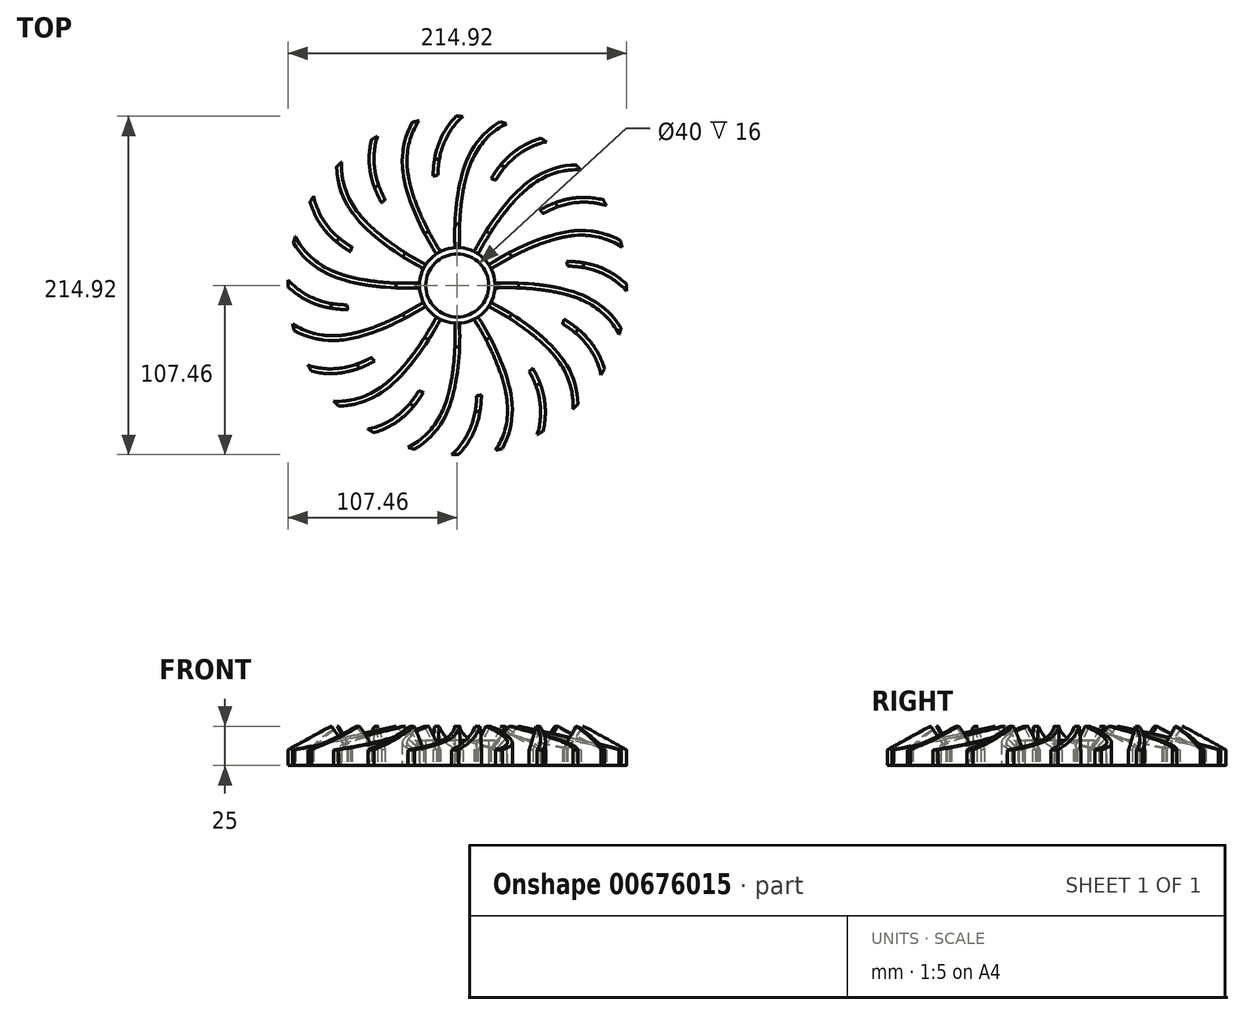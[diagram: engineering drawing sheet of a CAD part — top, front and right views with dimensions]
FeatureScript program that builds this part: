
annotation { "Feature Type Name" : "Feature", "Feature Type Description" : "" }
export const myFeature = defineFeature(function(context is Context, id is Id, definition is map)
    precondition{}
    {
        {
            var Q0;
            Q0=qCreatedBy(makeId("Top.planeOp"),FACE);
            var sketch = newSketch(context, id + "F0", { "sketchPlane" : qUnion([Q0])});
            skCircle(sketch, "E0", {"center": v(0, 0) * mm, "radius": 20 * mm});
            skArc(sketch, "E1", {"start": v(96, -28) * mm, "mid": v(71.3, -7.4) * mm, "end": v(40, 0) * mm});
            skArc(sketch, "E2.0", {"start": v(93.6, -29.8) * mm, "mid": v(69.96, -10.07) * mm, "end": v(40, -3) * mm});
            skLineSegment(sketch, "E3", {"start": v(40, 0) * mm, "end": v(40, -3) * mm});
            skLineSegment(sketch, "E4", {"start": v(93.6, -29.8) * mm, "end": v(96, -28) * mm});
            skCircle(sketch, "E5", {"center": v(0, 0) * mm, "radius": 24 * mm});
            skLineSegment(sketch, "E6", {"start": v(0, 24) * mm, "end": v(0, 20) * mm, "construction": true});
            skLineSegment(sketch, "E7", {"start": v(64.84, -4.56) * mm, "end": v(63.78, -7.36) * mm});
            skLineSegment(sketch, "E8", {"start": v(40, 0) * mm, "end": v(40, -70) * mm, "construction": true});
            skFitSpline(sketch, "E9", {"points": [v(24, 0) * mm, v(83, -9.5) * mm, v(106, -36.5) * mm], "startDerivative": vector(103.5, 1.7) * mm, "endDerivative": vector(16.54, -68.53) * mm, "construction": true});
            skLineSegment(sketch, "E10", {"start": v(-53.16, 0) * mm, "end": v(120.42, 0) * mm, "construction": true});
            skFitSpline(sketch, "E11.0", {"points": [v(23.98, 1.5) * mm, v(28.3, 1.57) * mm, v(37.36, 1.54) * mm, v(49.06, 0.79) * mm, v(58.28, -0.42) * mm, v(65.05, -1.67) * mm, v(71.58, -3.31) * mm, v(77.78, -5.4) * mm, v(83.57, -7.97) * mm, v(88.84, -11.08) * mm, v(93.54, -14.64) * mm, v(97.64, -18.56) * mm, v(101.12, -22.75) * mm, v(104.9, -28.6) * mm, v(106.73, -33.14) * mm, v(107.46, -36.15) * mm]});
            skFitSpline(sketch, "E12.0", {"points": [v(24.02, -1.5) * mm, v(28.32, -1.43) * mm, v(37.27, -1.46) * mm, v(48.79, -2.2) * mm, v(57.82, -3.38) * mm, v(64.42, -4.6) * mm, v(70.74, -6.2) * mm, v(76.7, -8.2) * mm, v(82.2, -10.65) * mm, v(87.17, -13.58) * mm, v(91.6, -16.93) * mm, v(95.45, -20.61) * mm, v(98.7, -24.53) * mm, v(102.22, -29.97) * mm, v(103.89, -34.15) * mm, v(104.54, -36.85) * mm]});
            skLineSegment(sketch, "E13", {"start": v(107.46, -36.15) * mm, "end": v(104.54, -36.85) * mm});
            skLineSegment(sketch, "E14", {"start": v(23.98, 1.5) * mm, "end": v(24.02, -1.5) * mm});
            skLineSegment(sketch, "E15", {"start": v(71.17, -3.28) * mm, "end": v(70.34, -6.17) * mm});
            skSolve(sketch);
        }
        {
            var Q0;
            Q0=makeQuery(id+"F0.imprint","IMPRINT",FACE,{"disambiguationData":[TD([[makeQuery(id+"F0.imprint","IMPRINT",EDGE,{"derivedFrom":sQuery(id+"F0.wireOp",EDGE,"E1")}),1.0]])]});
            var Q1;
            {var subQ13=sQuery(id+"F0.wireOp",EDGE,"E11.0");Q1=makeQuery(id+"F0.imprint","IMPRINT",FACE,{"disambiguationData":[TD([[makeQuery(id+"F0.imprint","IMPRINT",EDGE,{"derivedFrom":subQ13}),-1.0]])]});}
            var Q2;
            {var subQ0=sQuery(id+"F0.wireOp",EDGE,"E3");var subQ1=sQuery(id+"F0.wireOp",EDGE,"E1");var subQ2=makeQuery(id+"F0.imprint","INTERSECT",VERTEX,{"derivedFrom":[subQ1,subQ0]});Q2=makeQuery(id+"F0.imprint","IMPRINT",FACE,{"disambiguationData":[TD([[makeQuery(id+"F0.imprint","IMPRINT",EDGE,{"disambiguationData":[TD([[subQ2,1.0]])],"derivedFrom":subQ1}),1.0]])]});}
            var Q3;
            {var subQ13=sQuery(id+"F0.wireOp",EDGE,"E15");Q3=makeQuery(id+"F0.imprint","IMPRINT",FACE,{"disambiguationData":[TD([[makeQuery(id+"F0.imprint","IMPRINT",EDGE,{"derivedFrom":subQ13}),-1.0]])]});}
            extrude(context, id + "F1", {"entities" : qUnion([Q0, Q1, Q2, Q3]), "depth" : 25 * mm, "offsetDistance" : 25 * mm});
        }
        {
            var Q0;
            Q0=qCreatedBy(makeId("Front.planeOp"),FACE);
            var sketch = newSketch(context, id + "F2", { "sketchPlane" : qUnion([Q0])});
            skPoint(sketch, "E16", {"position": v(24, 25) * mm});
            skLineSegment(sketch, "E17", {"start": v(39, 25) * mm, "end": v(107.46, 10) * mm});
            skLineSegment(sketch, "E18", {"start": v(107.46, 10) * mm, "end": v(107.46, 0) * mm});
            skLineSegment(sketch, "E19", {"start": v(39, 25) * mm, "end": v(24, 10) * mm});
            skLineSegment(sketch, "E20", {"start": v(24, 10) * mm, "end": v(24, 0) * mm});
            skLineSegment(sketch, "E21", {"start": v(24, 0) * mm, "end": v(107.46, 0) * mm});
            skLineSegment(sketch, "E22", {"start": v(0, 26.68) * mm, "end": v(0, -26.42) * mm, "construction": true});
            skSolve(sketch);
        }
        {
            var Q0;
            Q0=makeQuery(id+"F2.imprint","IMPRINT",FACE,{"disambiguationData":[TD([[makeQuery(id+"F2.imprint","IMPRINT",EDGE,{"derivedFrom":sQuery(id+"F2.wireOp",EDGE,"E17")}),-1.0]])]});
            var Q1;
            Q1=sQuery(id+"F2.wireOp",EDGE,"E22");
            revolve(context, id + "F3", {"entities" : qUnion([Q0]), "axis" : qUnion([Q1]), "revolveType" : RevolveType.FULL});
        }
        {
            var Q0;
            Q0=makeQuery(id+"F1.opExtrude","SWEPT_BODY",BODY,{"disambiguationData":[OSD([sQuery(id+"F0.wireOp",EDGE,"E5"),sQuery(id+"F0.wireOp",EDGE,"E11.0"),sQuery(id+"F0.wireOp",EDGE,"E12.0"),sQuery(id+"F0.wireOp",EDGE,"E13"),sQuery(id+"F0.wireOp",EDGE,"E14")])]});
            var Q1;
            Q1=makeQuery(id+"F3.opRevolve","SWEPT_BODY",BODY,{"disambiguationData":[OSD([sQuery(id+"F2.wireOp",EDGE,"E17"),sQuery(id+"F2.wireOp",EDGE,"E18"),sQuery(id+"F2.wireOp",EDGE,"E19"),sQuery(id+"F2.wireOp",EDGE,"E20"),sQuery(id+"F2.wireOp",EDGE,"E21")])]});
            booleanBodies(context, id + "F4", {"operationType" : BooleanOperationType.INTERSECTION, "tools" : qUnion([Q0, Q1])});
        }
        {
            var Q0;
            {var subQ0=sQuery(id+"F0.wireOp",EDGE,"E13");Q0=makeQuery(id+"F0.imprint","IMPRINT",FACE,{"disambiguationData":[TD([[makeQuery(id+"F0.imprint","IMPRINT",EDGE,{"derivedFrom":subQ0}),-1.0]])]});}
            extrude(context, id + "F5", {"entities" : qUnion([Q0]), "depth" : 25 * mm, "offsetDistance" : 25 * mm});
        }
        {
            var Q0;
            Q0=qCreatedBy(makeId("Front.planeOp"),FACE);
            var sketch = newSketch(context, id + "F6", { "sketchPlane" : qUnion([Q0])});
            skLineSegment(sketch, "E23", {"start": v(71.17, 0) * mm, "end": v(71.17, 10) * mm});
            skLineSegment(sketch, "E24", {"start": v(71.17, 10) * mm, "end": v(81.17, 25) * mm});
            skLineSegment(sketch, "E25", {"start": v(81.17, 25) * mm, "end": v(107.46, 10) * mm});
            skLineSegment(sketch, "E26", {"start": v(107.46, 10) * mm, "end": v(107.46, 0) * mm});
            skLineSegment(sketch, "E27", {"start": v(107.46, 0) * mm, "end": v(71.17, 0) * mm});
            skPoint(sketch, "E28", {"position": v(71.17, 25) * mm});
            skSolve(sketch);
        }
        {
            var Q0;
            Q0=makeQuery(id+"F6.imprint","IMPRINT",FACE,{"disambiguationData":[TD([[makeQuery(id+"F6.imprint","IMPRINT",EDGE,{"derivedFrom":sQuery(id+"F6.wireOp",EDGE,"E23")}),-1.0]])]});
            var Q1;
            Q1=sQuery(id+"F2.wireOp",EDGE,"E22");
            revolve(context, id + "F7", {"entities" : qUnion([Q0]), "axis" : qUnion([Q1]), "revolveType" : RevolveType.FULL});
        }
        {
            var Q0;
            Q0=makeQuery(id+"F7.opRevolve","SWEPT_BODY",BODY,{"disambiguationData":[OSD([sQuery(id+"F6.wireOp",EDGE,"E23"),sQuery(id+"F6.wireOp",EDGE,"E24"),sQuery(id+"F6.wireOp",EDGE,"E25"),sQuery(id+"F6.wireOp",EDGE,"E26"),sQuery(id+"F6.wireOp",EDGE,"E27")])]});
            var Q1;
            Q1=makeQuery(id+"F5.opExtrude","SWEPT_BODY",BODY,{"disambiguationData":[OSD([sQuery(id+"F0.wireOp",EDGE,"E11.0"),sQuery(id+"F0.wireOp",EDGE,"E12.0"),sQuery(id+"F0.wireOp",EDGE,"E13"),sQuery(id+"F0.wireOp",EDGE,"E15")])]});
            booleanBodies(context, id + "F8", {"operationType" : BooleanOperationType.INTERSECTION, "tools" : qUnion([Q0, Q1])});
        }
        {
            var Q0;
            Q0=makeQuery(id+"F8.opBoolean","INTERSECT",BODY,{"derivedFrom":[makeQuery(id+"F5.opExtrude","SWEPT_BODY",BODY,{"disambiguationData":[OSD([sQuery(id+"F0.wireOp",EDGE,"E11.0"),sQuery(id+"F0.wireOp",EDGE,"E12.0"),sQuery(id+"F0.wireOp",EDGE,"E13"),sQuery(id+"F0.wireOp",EDGE,"E15")])]}),makeQuery(id+"F7.opRevolve","SWEPT_BODY",BODY,{"disambiguationData":[OSD([sQuery(id+"F6.wireOp",EDGE,"E23"),sQuery(id+"F6.wireOp",EDGE,"E24"),sQuery(id+"F6.wireOp",EDGE,"E25"),sQuery(id+"F6.wireOp",EDGE,"E26"),sQuery(id+"F6.wireOp",EDGE,"E27")])]})]});
            var Q1;
            Q1=sQuery(id+"F2.wireOp",EDGE,"E22");
            transform(context, id + "F9", {"entities" : qUnion([Q0]), "transformType" : TransformType.ROTATION, "transformAxis" : qUnion([Q1]), "angle" : 15 * degree, "makeCopy" : false});
        }
        {
            var Q0;
            Q0=makeQuery(id+"F4.opBoolean","INTERSECT",BODY,{"derivedFrom":[makeQuery(id+"F1.opExtrude","SWEPT_BODY",BODY,{"disambiguationData":[OSD([sQuery(id+"F0.wireOp",EDGE,"E5"),sQuery(id+"F0.wireOp",EDGE,"E11.0"),sQuery(id+"F0.wireOp",EDGE,"E12.0"),sQuery(id+"F0.wireOp",EDGE,"E13"),sQuery(id+"F0.wireOp",EDGE,"E14")])]}),makeQuery(id+"F3.opRevolve","SWEPT_BODY",BODY,{"disambiguationData":[OSD([sQuery(id+"F2.wireOp",EDGE,"E17"),sQuery(id+"F2.wireOp",EDGE,"E18"),sQuery(id+"F2.wireOp",EDGE,"E19"),sQuery(id+"F2.wireOp",EDGE,"E20"),sQuery(id+"F2.wireOp",EDGE,"E21")])]})]});
            var Q1;
            Q1=sQuery(id+"F2.wireOp",EDGE,"E22");
            circularPattern(context, id + "F10", {"entities" : qUnion([Q0]), "axis" : qUnion([Q1]), "angle" : 360 * degree, "instanceCount" : 12, "equalSpace" : true});
        }
        {
            var Q0;
            Q0=makeQuery(id+"F8.opBoolean","INTERSECT",BODY,{"derivedFrom":[makeQuery(id+"F5.opExtrude","SWEPT_BODY",BODY,{"disambiguationData":[OSD([sQuery(id+"F0.wireOp",EDGE,"E11.0"),sQuery(id+"F0.wireOp",EDGE,"E12.0"),sQuery(id+"F0.wireOp",EDGE,"E13"),sQuery(id+"F0.wireOp",EDGE,"E15")])]}),makeQuery(id+"F7.opRevolve","SWEPT_BODY",BODY,{"disambiguationData":[OSD([sQuery(id+"F6.wireOp",EDGE,"E23"),sQuery(id+"F6.wireOp",EDGE,"E24"),sQuery(id+"F6.wireOp",EDGE,"E25"),sQuery(id+"F6.wireOp",EDGE,"E26"),sQuery(id+"F6.wireOp",EDGE,"E27")])]})]});
            var Q1;
            Q1=sQuery(id+"F2.wireOp",EDGE,"E22");
            circularPattern(context, id + "F11", {"entities" : qUnion([Q0]), "axis" : qUnion([Q1]), "angle" : 360 * degree, "instanceCount" : 12, "equalSpace" : true});
        }
        {
            var Q0;
            Q0=makeQuery(id+"F0.imprint","IMPRINT",FACE,{"disambiguationData":[TD([[makeQuery(id+"F0.imprint","IMPRINT",EDGE,{"derivedFrom":sQuery(id+"F0.wireOp",EDGE,"E0")}),-1.0]])]});
            extrude(context, id + "F12", {"entities" : qUnion([Q0]), "depth" : 16 * mm, "offsetDistance" : 25 * mm});
        }
    });
